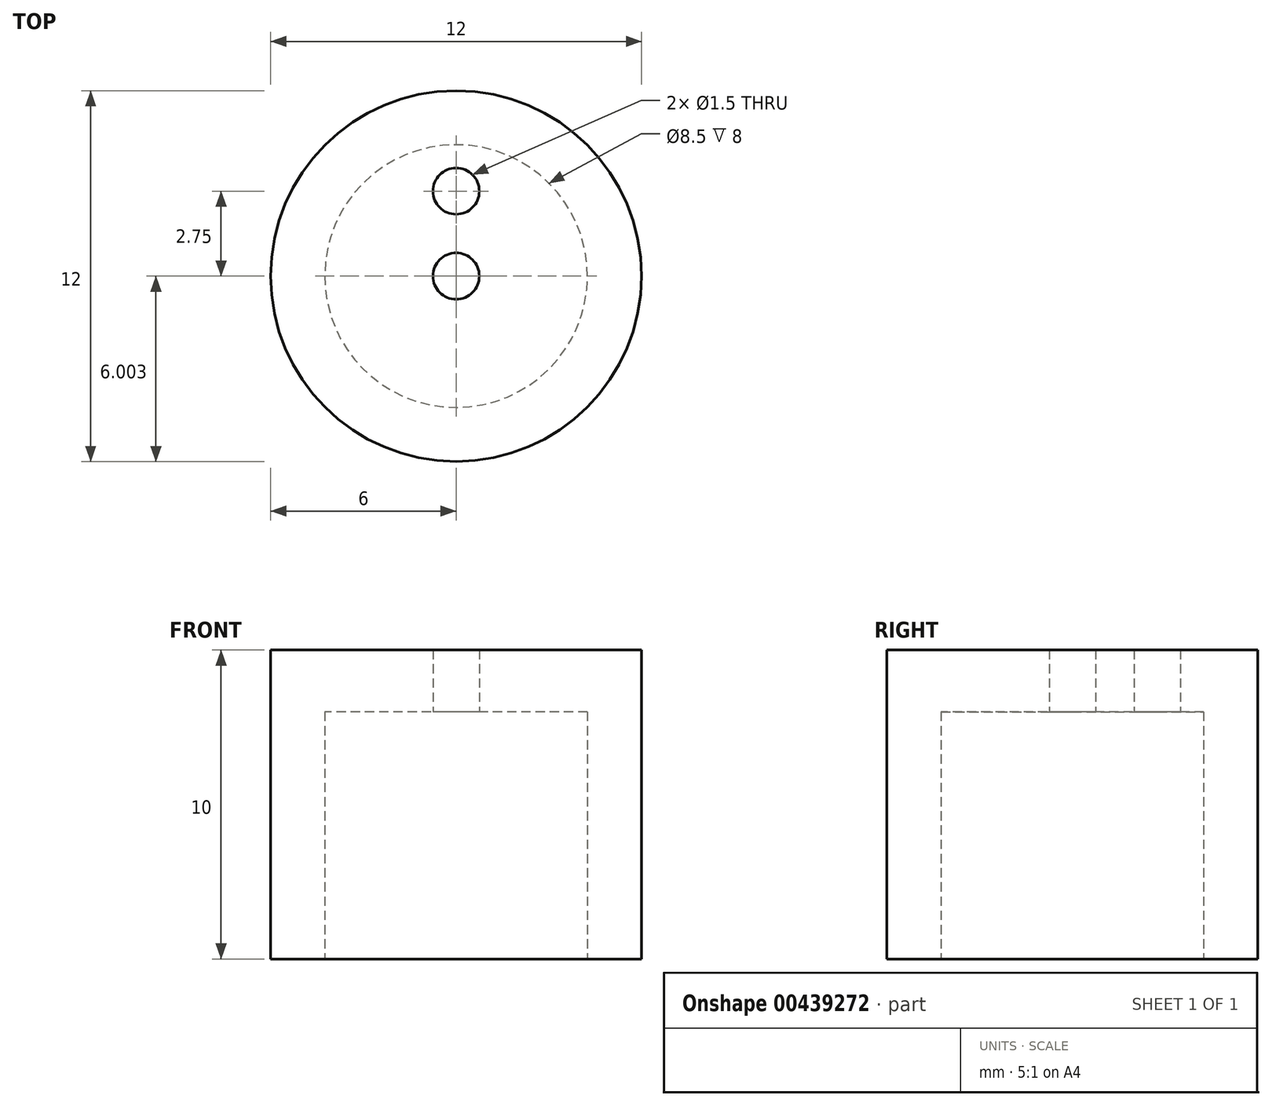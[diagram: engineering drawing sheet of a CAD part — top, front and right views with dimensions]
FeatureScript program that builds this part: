
annotation { "Feature Type Name" : "Feature", "Feature Type Description" : "" }
export const myFeature = defineFeature(function(context is Context, id is Id, definition is map)
    precondition{}
    {
        {
            var Q0;
            Q0=qCreatedBy(makeId("Top.planeOp"),FACE);
            var sketch = newSketch(context, id + "F0", { "sketchPlane" : qUnion([Q0])});
            skCircle(sketch, "E0", {"center": v(0, -0.55) * mm, "radius": 6 * mm});
            skCircle(sketch, "E1", {"center": v(0, -0.55) * mm, "radius": 4.25 * mm});
            skPoint(sketch, "E2", {"position": v(0, 2.2) * mm});
            skSolve(sketch);
        }
        {
            var Q0;
            Q0=makeQuery(id+"F0.imprint","IMPRINT",FACE,{"disambiguationData":[TD([[makeQuery(id+"F0.imprint","IMPRINT",EDGE,{"derivedFrom":sQuery(id+"F0.wireOp",EDGE,"E0")}),1.0]])]});
            var Q1;
            Q1=makeQuery(id+"F0.imprint","IMPRINT",FACE,{"disambiguationData":[TD([[makeQuery(id+"F0.imprint","IMPRINT",EDGE,{"derivedFrom":sQuery(id+"F0.wireOp",EDGE,"E1")}),1.0]])]});
            extrude(context, id + "F1", {"entities" : qUnion([Q0, Q1]), "depth" : 10 * mm});
        }
        {
            var Q0;
            Q0=makeQuery(id+"F0.imprint","IMPRINT",FACE,{"disambiguationData":[TD([[makeQuery(id+"F0.imprint","IMPRINT",EDGE,{"derivedFrom":sQuery(id+"F0.wireOp",EDGE,"E1")}),1.0]])]});
            extrude(context, id + "F2", {"entities" : qUnion([Q0]), "operationType" : NewBodyOperationType.REMOVE, "depth" : 8 * mm});
        }
        {
            var Q0;
            Q0=sQuery(id+"F0.wireOp",VERTEX,"E0.center");
            var Q1;
            Q1=sQuery(id+"F0.wireOp",VERTEX,"E2");
            var Q2;
            Q2=makeQuery(id+"F1.opExtrude","SWEPT_BODY",BODY,{"disambiguationData":[OSD([sQuery(id+"F0.wireOp",EDGE,"E0")])]});
            hole(context, id + "F3", {"style" : HoleStyle.SIMPLE, "endStyle" : HoleEndStyle.THROUGH, "oppositeDirection" : true, "holeDiameter" : 1.5 * mm, "isTappedThrough" : true, "tappedDepth" : 12 * mm, "tapClearance" : 3, "locations" : qUnion([Q0, Q1]), "scope" : qUnion([Q2])});
        }
    });
